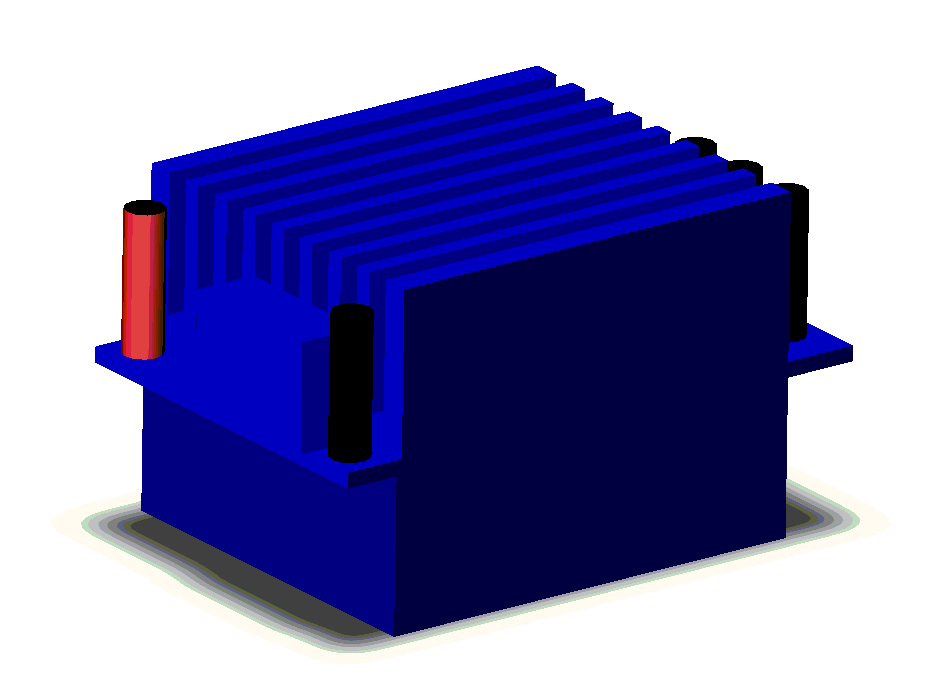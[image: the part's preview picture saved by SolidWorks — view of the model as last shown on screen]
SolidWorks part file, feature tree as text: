
SOLIDWORKS PART (.sldprt)
format: sldprt  version: not decoded by parser v0  size: 510,976 bytes
history: native  units: mm
features: sketch x6, extrude x5, cut_extrude x1, pattern_linear x1 (+8 scaffold rows collapsed)
feature tree (21):
  scaffold x8  (default folders/planes/origin — collapsed)
  sketch  "Sketch1"  dims[D1=27.5mm D2=31.5mm]
  extrude  "Base-Extrude"  Depth=11.12mm
  sketch  "Sketch2"  dims[D1=3.94mm D2=40.63mm]
  extrude  "Boss-Extrude1"  Depth=1.1mm
  sketch  "Sketch3"  dims[D1=24.0mm]
  extrude  "Boss-Extrude2"  Depth=31.1mm
  sketch  "Sketch4"  dims[D1=1.76mm D2=3.0mm D3=2.0mm]
  cut_extrude  "Cut-Extrude1"  [1 undecoded]
  pattern_linear  "LPattern1"  Count1=8 Count2=1 Spacing1=3.1mm Spacing2=50mm
  sketch  "Sketch5"  dims[D1=2.85mm D4=2.85mm D7=2.85mm D11=2.85mm D12=2.85mm D2=2.0mm D3=2.5mm D5=2.5mm D6=2.0mm D8=4.0mm D9=5.0mm D10=5.0mm]
  extrude  "Boss-Extrude3"  Depth=10mm
  sketch  "Sketch6"
  extrude  "Boss-Extrude4"  Depth=7.8mm
decode coverage: 11 of 13 modeling features carry decoded parameters
note: 1 parameter value undecoded
note: suppression state not decoded; provenance and decode notes live in map.json
